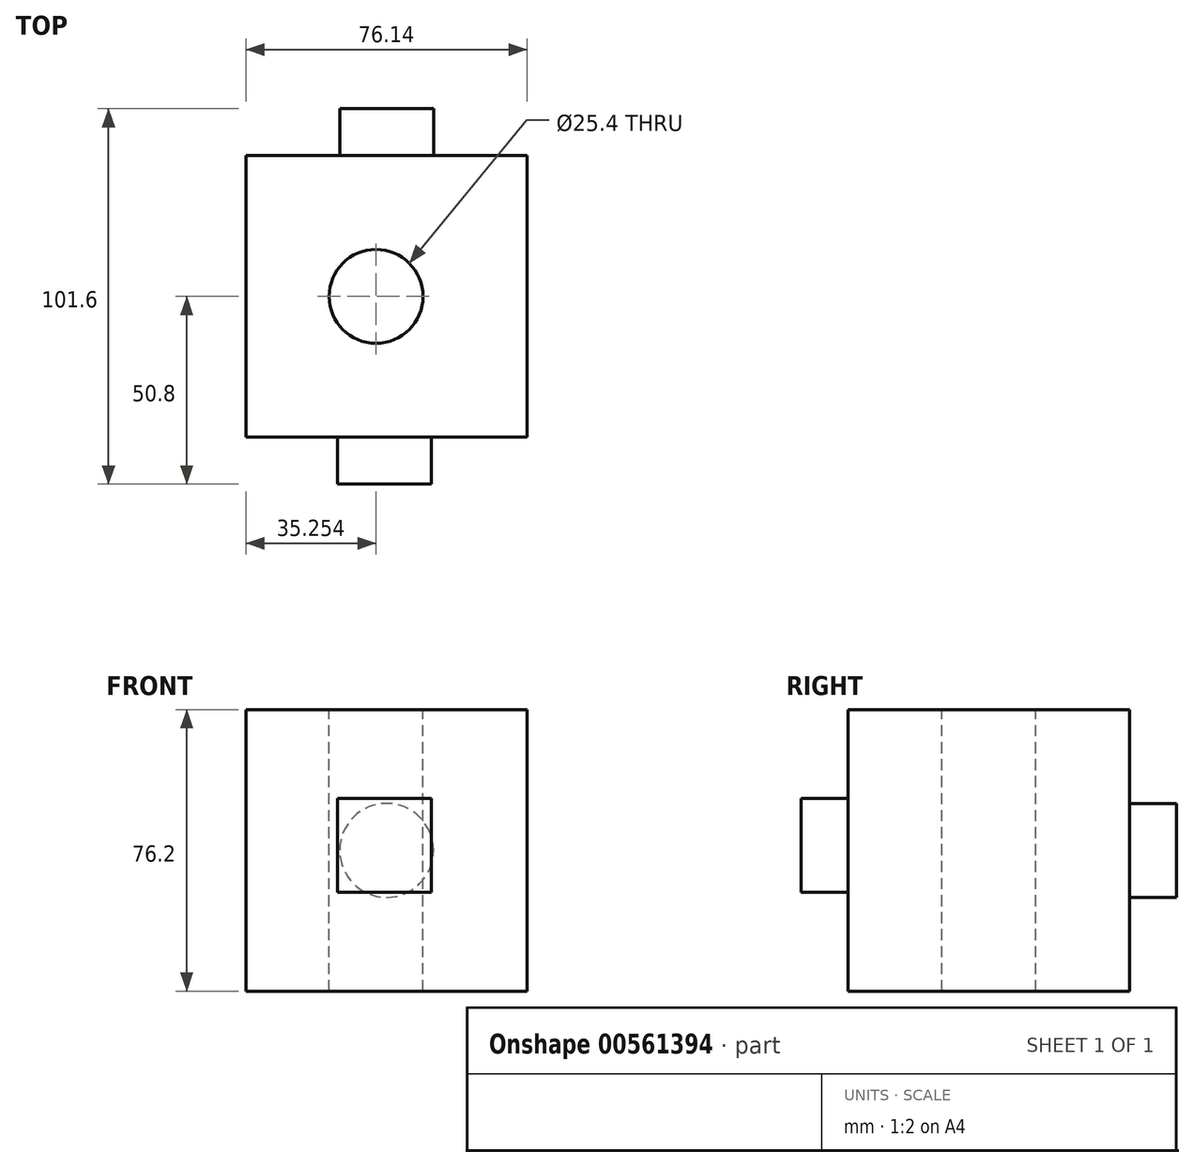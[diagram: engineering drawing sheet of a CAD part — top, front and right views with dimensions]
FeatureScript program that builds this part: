
annotation { "Feature Type Name" : "Feature", "Feature Type Description" : "" }
export const myFeature = defineFeature(function(context is Context, id is Id, definition is map)
    precondition{}
    {
        {
            var Q0;
            Q0=qCreatedBy(makeId("Front.planeOp"),FACE);
            var sketch = newSketch(context, id + "F0", { "sketchPlane" : qUnion([Q0])});
            skLineSegment(sketch, "E0.bottom", {"start": v(0, 0) * mm, "end": v(76.14, 0) * mm});
            skLineSegment(sketch, "E0.top", {"start": v(0, 76.2) * mm, "end": v(76.14, 76.2) * mm});
            skLineSegment(sketch, "E0.left", {"start": v(0, 0) * mm, "end": v(0, 76.2) * mm});
            skLineSegment(sketch, "E0.right", {"start": v(76.14, 0) * mm, "end": v(76.14, 76.2) * mm});
            skSolve(sketch);
        }
        {
            var Q0;
            Q0 = qSketchRegion(id + "F0", true);
            extrude(context, id + "F1", {"entities" : qUnion([Q0]), "depth" : 76.2 * mm, "offsetDistance" : 25.4 * mm});
        }
        {
            var Q0;
            Q0=makeQuery(id+"F1.opExtrude","CAP_FACE",FACE,{"disambiguationData":[OSD([sQuery(id+"F0.wireOp",EDGE,"E0.bottom"),sQuery(id+"F0.wireOp",EDGE,"E0.top"),sQuery(id+"F0.wireOp",EDGE,"E0.left"),sQuery(id+"F0.wireOp",EDGE,"E0.right")])],"isStart":false});
            var sketch = newSketch(context, id + "F2", { "sketchPlane" : qUnion([Q0])});
            skLineSegment(sketch, "E1.bottom", {"start": v(24.83, 26.74) * mm, "end": v(50.23, 26.74) * mm});
            skLineSegment(sketch, "E1.top", {"start": v(24.83, 52.14) * mm, "end": v(50.23, 52.14) * mm});
            skLineSegment(sketch, "E1.left", {"start": v(24.83, 26.74) * mm, "end": v(24.83, 52.14) * mm});
            skLineSegment(sketch, "E1.right", {"start": v(50.23, 26.74) * mm, "end": v(50.23, 52.14) * mm});
            skSolve(sketch);
        }
        {
            var Q0;
            Q0=makeQuery(id+"F1.opExtrude","SWEPT_FACE",FACE,{"disambiguationData":[OSD([sQuery(id+"F0.wireOp",EDGE,"E0.top")])]});
            var sketch = newSketch(context, id + "F3", { "sketchPlane" : qUnion([Q0])});
            skPoint(sketch, "E2", {"position": v(35.25, -38.1) * mm});
            skPoint(sketch, "E2.positionSnap0", {"position": v(0, -38.1) * mm});
            skSolve(sketch);
        }
        {
            var Q0;
            Q0=sQuery(id+"F3.wireOp",VERTEX,"E2");
            var Q1;
            Q1=makeQuery(id+"F1.opExtrude","SWEPT_BODY",BODY,{"disambiguationData":[OSD([sQuery(id+"F0.wireOp",EDGE,"E0.bottom"),sQuery(id+"F0.wireOp",EDGE,"E0.top"),sQuery(id+"F0.wireOp",EDGE,"E0.left"),sQuery(id+"F0.wireOp",EDGE,"E0.right")])]});
            hole(context, id + "F4", {"style" : HoleStyle.SIMPLE, "endStyle" : HoleEndStyle.THROUGH, "holeDiameter" : 25.4 * mm, "isTappedThrough" : true, "tappedDepth" : 12.7 * mm, "tapClearance" : 3, "locations" : qUnion([Q0]), "scope" : qUnion([Q1])});
        }
        {
            var Q0;
            Q0=makeQuery(id+"F2.imprint","IMPRINT",FACE,{"disambiguationData":[TD([[makeQuery(id+"F2.imprint","IMPRINT",EDGE,{"derivedFrom":sQuery(id+"F2.wireOp",EDGE,"E1.bottom")}),1.0]])]});
            extrude(context, id + "F5", {"entities" : qUnion([Q0]), "operationType" : NewBodyOperationType.ADD, "depth" : 12.7 * mm, "offsetDistance" : 25.4 * mm});
        }
        {
            var Q0;
            Q0=makeQuery(id+"F1.opExtrude","CAP_FACE",FACE,{"disambiguationData":[OSD([sQuery(id+"F0.wireOp",EDGE,"E0.bottom"),sQuery(id+"F0.wireOp",EDGE,"E0.top"),sQuery(id+"F0.wireOp",EDGE,"E0.left"),sQuery(id+"F0.wireOp",EDGE,"E0.right")])],"isStart":true});
            var sketch = newSketch(context, id + "F6", { "sketchPlane" : qUnion([Q0])});
            skCircle(sketch, "E3", {"center": v(-38.1, 38.1) * mm, "radius": 12.7 * mm});
            skSolve(sketch);
        }
        {
            var Q0;
            Q0=makeQuery(id+"F6.imprint","IMPRINT",FACE,{"disambiguationData":[TD([[makeQuery(id+"F6.imprint","IMPRINT",EDGE,{"derivedFrom":sQuery(id+"F6.wireOp",EDGE,"E3")}),1.0]])]});
            extrude(context, id + "F7", {"entities" : qUnion([Q0]), "operationType" : NewBodyOperationType.ADD, "depth" : 12.7 * mm, "offsetDistance" : 25.4 * mm});
        }
    });
